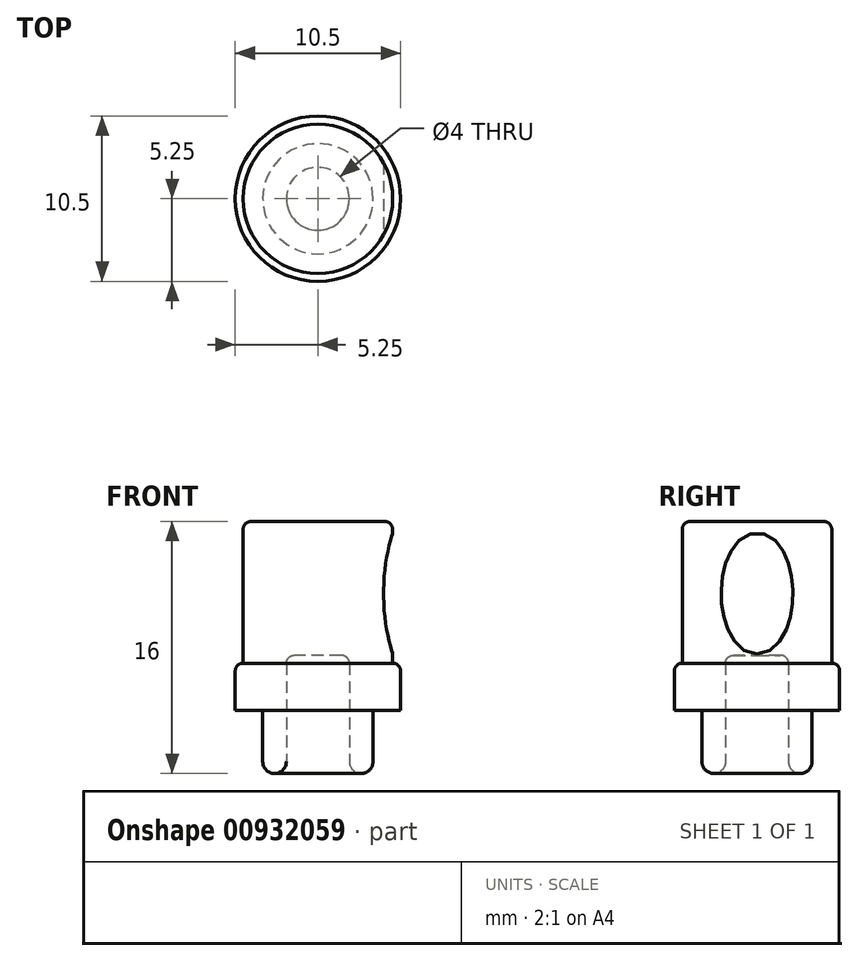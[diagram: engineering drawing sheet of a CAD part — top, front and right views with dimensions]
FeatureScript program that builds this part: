
annotation { "Feature Type Name" : "Feature", "Feature Type Description" : "" }
export const myFeature = defineFeature(function(context is Context, id is Id, definition is map)
    precondition{}
    {
        {
            var Q0;
            Q0=qCreatedBy(makeId("Front.planeOp"),FACE);
            var sketch = newSketch(context, id + "F0", { "sketchPlane" : qUnion([Q0])});
            skLineSegment(sketch, "E0", {"start": v(0, 0) * mm, "end": v(0, 31.55) * mm, "construction": true});
            skLineSegment(sketch, "E1", {"start": v(2, 0) * mm, "end": v(3.5, 0) * mm});
            skLineSegment(sketch, "E2", {"start": v(3.5, 0) * mm, "end": v(3.5, 4) * mm});
            skLineSegment(sketch, "E3", {"start": v(3.5, 4) * mm, "end": v(5.25, 4) * mm});
            skLineSegment(sketch, "E4", {"start": v(5.25, 4) * mm, "end": v(5.25, 7) * mm});
            skLineSegment(sketch, "E5", {"start": v(5.25, 7) * mm, "end": v(4.75, 7) * mm});
            skLineSegment(sketch, "E6", {"start": v(4.75, 7) * mm, "end": v(4.75, 16) * mm});
            skLineSegment(sketch, "E7", {"start": v(4.75, 16) * mm, "end": v(0, 16) * mm});
            skLineSegment(sketch, "E8", {"start": v(2, 0) * mm, "end": v(2, 7.5) * mm});
            skLineSegment(sketch, "E9", {"start": v(2, 7.5) * mm, "end": v(0, 7.5) * mm});
            skLineSegment(sketch, "E10", {"start": v(0, 16) * mm, "end": v(0, 7.5) * mm});
            skLineSegment(sketch, "E11", {"start": v(-2.28, 15.28) * mm, "end": v(12.5, 15.28) * mm, "construction": true});
            skLineSegment(sketch, "E12", {"start": v(-2.28, 7.59) * mm, "end": v(12.79, 7.59) * mm, "construction": true});
            skArc(sketch, "E13", {"start": v(4.75, 15.28) * mm, "mid": v(4.17, 11.43) * mm, "end": v(4.75, 7.59) * mm});
            skLineSegment(sketch, "E14", {"start": v(4.75, 15.28) * mm, "end": v(6.48, 15.28) * mm});
            skLineSegment(sketch, "E15", {"start": v(6.48, 15.28) * mm, "end": v(6.48, 7.59) * mm});
            skLineSegment(sketch, "E16", {"start": v(6.48, 7.59) * mm, "end": v(4.75, 7.59) * mm});
            skSolve(sketch);
        }
        {
            var Q0;
            Q0=makeQuery(id+"F0.imprint","IMPRINT",FACE,{"disambiguationData":[TD([[makeQuery(id+"F0.imprint","IMPRINT",EDGE,{"derivedFrom":sQuery(id+"F0.wireOp",EDGE,"E1")}),1.0]])]});
            var Q1;
            {var subQ0=sQuery(id+"F0.wireOp",EDGE,"E13");Q1=makeQuery(id+"F0.imprint","IMPRINT",FACE,{"disambiguationData":[TD([[makeQuery(id+"F0.imprint","IMPRINT",EDGE,{"derivedFrom":subQ0}),1.0]])]});}
            var Q2;
            Q2=sQuery(id+"F0.wireOp",EDGE,"E0");
            revolve(context, id + "F1", {"surfaceOperationType" : NewSurfaceOperationType.NEW, "entities" : qUnion([Q0, Q1]), "axis" : qUnion([Q2]), "revolveType" : RevolveType.FULL});
        }
        {
            var Q0;
            Q0=makeQuery(id+"F1.opRevolve","SWEPT_EDGE",EDGE,{"disambiguationData":[OSD([sQuery(id+"F0.wireOp",EDGE,"E6"),sQuery(id+"F0.wireOp",EDGE,"E7")])]});
            var Q1;
            Q1=makeQuery(id+"F1.opRevolve","SWEPT_EDGE",EDGE,{"disambiguationData":[OSD([sQuery(id+"F0.wireOp",EDGE,"E4"),sQuery(id+"F0.wireOp",EDGE,"E5")])]});
            var Q2;
            Q2=makeQuery(id+"F1.opRevolve","SWEPT_EDGE",EDGE,{"disambiguationData":[OSD([sQuery(id+"F0.wireOp",EDGE,"E8"),sQuery(id+"F0.wireOp",EDGE,"E9")])]});
            fillet(context, id + "F2", {"entities" : qUnion([Q0, Q1, Q2]), "radius" : .5 * mm, "tangentPropagation" : true, "allowEdgeOverflow" : false});
        }
        {
            var Q0;
            Q0=makeQuery(id+"F1.opRevolve","SWEPT_FACE",FACE,{"disambiguationData":[OSD([sQuery(id+"F0.wireOp",EDGE,"E1")])]});
            fillet(context, id + "F3", {"entities" : qUnion([Q0]), "radius" : 1.5 / 2 * mm, "tangentPropagation" : true, "allowEdgeOverflow" : false});
        }
        {
            var Q0;
            {var subQ0=sQuery(id+"F0.wireOp",EDGE,"E13");Q0=makeQuery(id+"F0.imprint","IMPRINT",FACE,{"disambiguationData":[TD([[makeQuery(id+"F0.imprint","IMPRINT",EDGE,{"derivedFrom":subQ0}),1.0]])]});}
            extrude(context, id + "F4", {"entities" : qUnion([Q0]), "operationType" : NewBodyOperationType.REMOVE, "endBound" : BoundingType.THROUGH_ALL, "oppositeDirection" : true, "depth" : 25 * mm, "offsetDistance" : 25 * mm, "hasSecondDirection" : true, "secondDirectionBound" : SecondDirectionBoundingType.THROUGH_ALL, "secondDirectionOppositeDirection" : false, "secondDirectionDepth" : 25 * mm});
        }
    });
